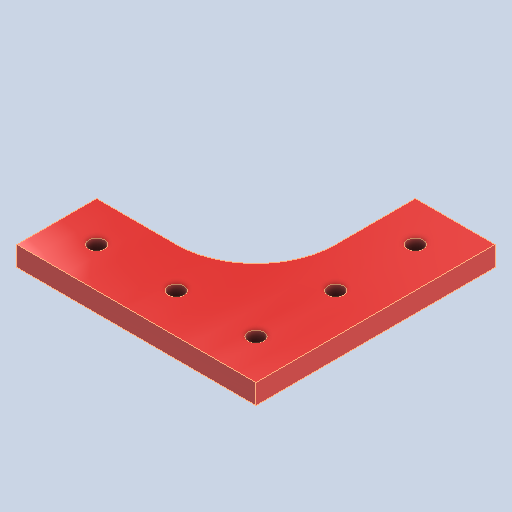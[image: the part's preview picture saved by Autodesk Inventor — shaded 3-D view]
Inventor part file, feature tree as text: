
AUTODESK INVENTOR PART (.ipt)
format: ipt  version: 2023 (Build 270158000, 158)  size: 132,608 bytes
history: native  units: in
note: dims shown in document units (in); Inventor stores cm internally (conversion verified against a paired STEP export)
features: extrude x1, sketch x1
ambient origin geometry x8: Origin, YZ Plane, XZ Plane, XY Plane, X Axis, Y Axis, Z Axis, Center Point
bodies: Solid1 (feature_tree)
feature tree (2):
  extrude  "Extrusion1"  Depth=1.0in
  sketch  "Sketch1"  dims[d0=3.0in d1=1.0in d2=1.0in d3=3.0in d4=1.0in d5=0.1969in d6=0.1969in d7=0.1969in d8=0.1969in d9=0.1969in d10=0.5in d11=0.5in d12=0.5in d13=0.5in d14=0.5in d15=0.5in d16=1.5in d17=1.5in d18=0.5in d19=0.5in d20=0.25in d21=0.0in]
